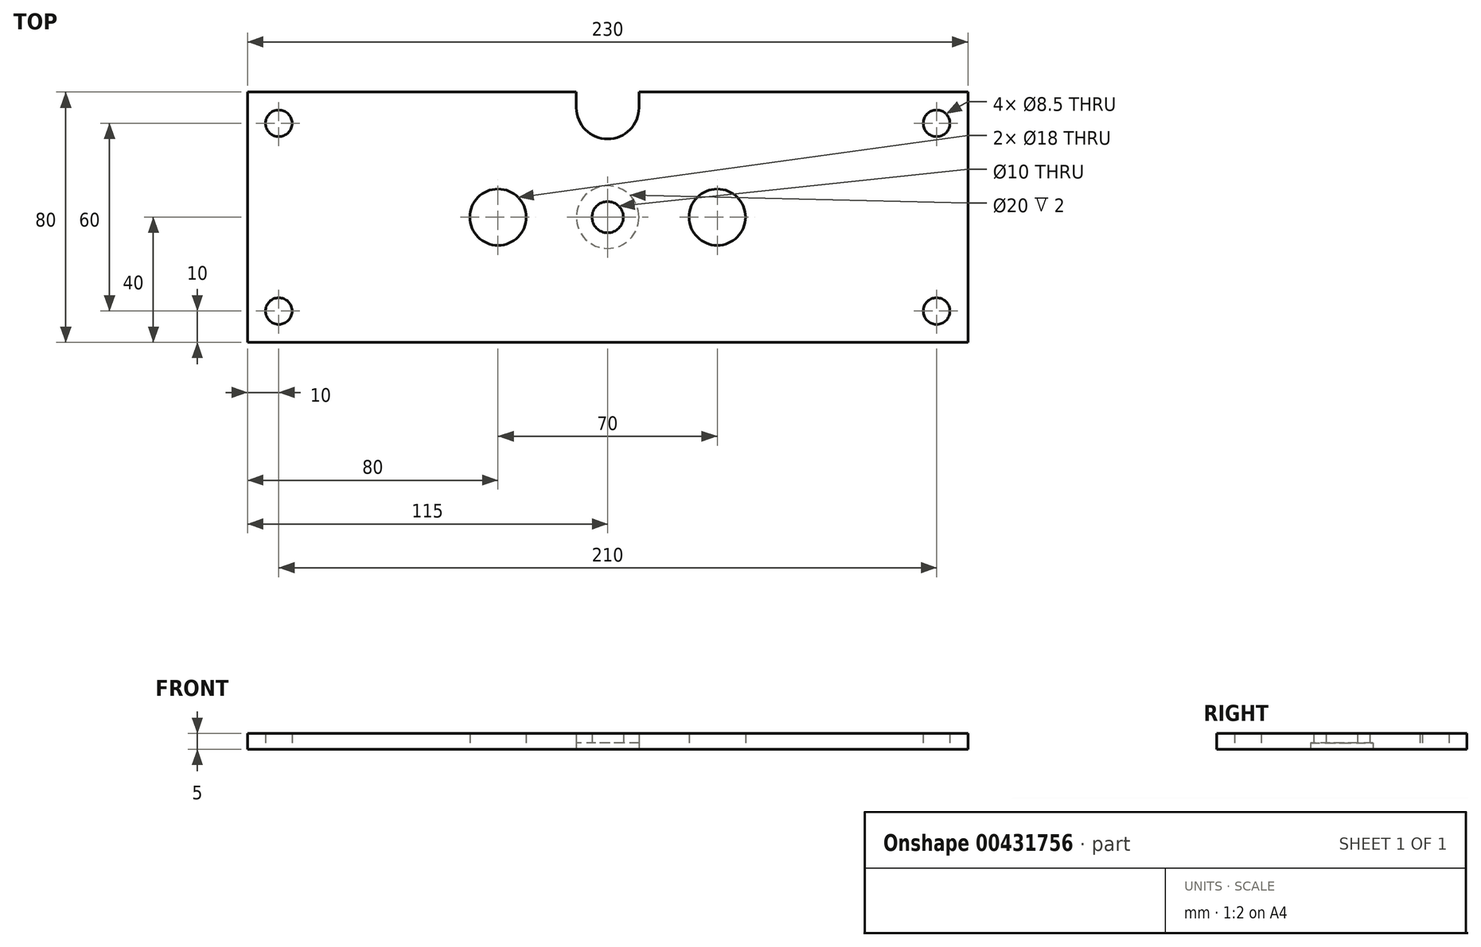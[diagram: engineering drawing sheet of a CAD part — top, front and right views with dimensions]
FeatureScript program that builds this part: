
annotation { "Feature Type Name" : "Feature", "Feature Type Description" : "" }
export const myFeature = defineFeature(function(context is Context, id is Id, definition is map)
    precondition{}
    {
        {
            var Q0;
            Q0=qCreatedBy(makeId("Top.planeOp"),FACE);
            var sketch = newSketch(context, id + "F0", { "sketchPlane" : qUnion([Q0])});
            skLineSegment(sketch, "E0.bottom", {"start": v(115, 40) * mm, "end": v(-115, 40) * mm});
            skLineSegment(sketch, "E0.top", {"start": v(115, -40) * mm, "end": v(-115, -40) * mm});
            skLineSegment(sketch, "E0.left", {"start": v(115, 40) * mm, "end": v(115, -40) * mm});
            skLineSegment(sketch, "E0.right", {"start": v(-115, 40) * mm, "end": v(-115, -40) * mm});
            skPoint(sketch, "E0.middle", {"position": v(0, 0) * mm});
            skCircle(sketch, "E1", {"center": v(-105, 30) * mm, "radius": 4.25 * mm});
            skCircle(sketch, "E2", {"center": v(105, 30) * mm, "radius": 4.25 * mm});
            skCircle(sketch, "E3", {"center": v(-35, 0) * mm, "radius": 9 * mm});
            skCircle(sketch, "E4", {"center": v(35, 0) * mm, "radius": 9 * mm});
            skCircle(sketch, "E5", {"center": v(0, 0) * mm, "radius": 5 * mm});
            skPoint(sketch, "E6.centerSnap0", {"position": v(0, 40) * mm});
            skLineSegment(sketch, "E7", {"start": v(-10, 40) * mm, "end": v(-10, 35) * mm});
            skLineSegment(sketch, "E8", {"start": v(10, 40) * mm, "end": v(10, 35) * mm});
            skArc(sketch, "E9", {"start": v(10, 35) * mm, "mid": v(0, 25) * mm, "end": v(-10, 35) * mm});
            skLineSegment(sketch, "E10", {"start": v(10, 40) * mm, "end": v(-10, 40) * mm});
            skCircle(sketch, "E11", {"center": v(-105, -30) * mm, "radius": 4.25 * mm});
            skCircle(sketch, "E12.MirrorC", {"center": v(105, -30) * mm, "radius": 4.25 * mm});
            skSolve(sketch);
        }
        {
            var Q0;
            Q0=makeQuery(id+"F0.imprint","IMPRINT",FACE,{"disambiguationData":[TD([[makeQuery(id+"F0.imprint","IMPRINT",EDGE,{"derivedFrom":sQuery(id+"F0.wireOp",EDGE,"E0.top")}),-1.0]])]});
            extrude(context, id + "F1", {"entities" : qUnion([Q0]), "depth" : 5 * mm});
        }
        {
            var Q0;
            Q0=makeQuery(id+"F0.imprint","IMPRINT",FACE,{"disambiguationData":[TD([[makeQuery(id+"F0.imprint","IMPRINT",EDGE,{"derivedFrom":sQuery(id+"F0.wireOp",EDGE,"E0.top")}),-1.0]])]});
            var sketch = newSketch(context, id + "F2", { "sketchPlane" : qUnion([Q0])});
            skCircle(sketch, "E13", {"center": v(0, 0) * mm, "radius": 10 * mm});
            skSolve(sketch);
        }
        {
            var Q0;
            Q0 = qSketchRegion(id + "F2", true);
            extrude(context, id + "F3", {"entities" : qUnion([Q0]), "operationType" : NewBodyOperationType.REMOVE, "depth" : 2 * mm});
        }
    });
